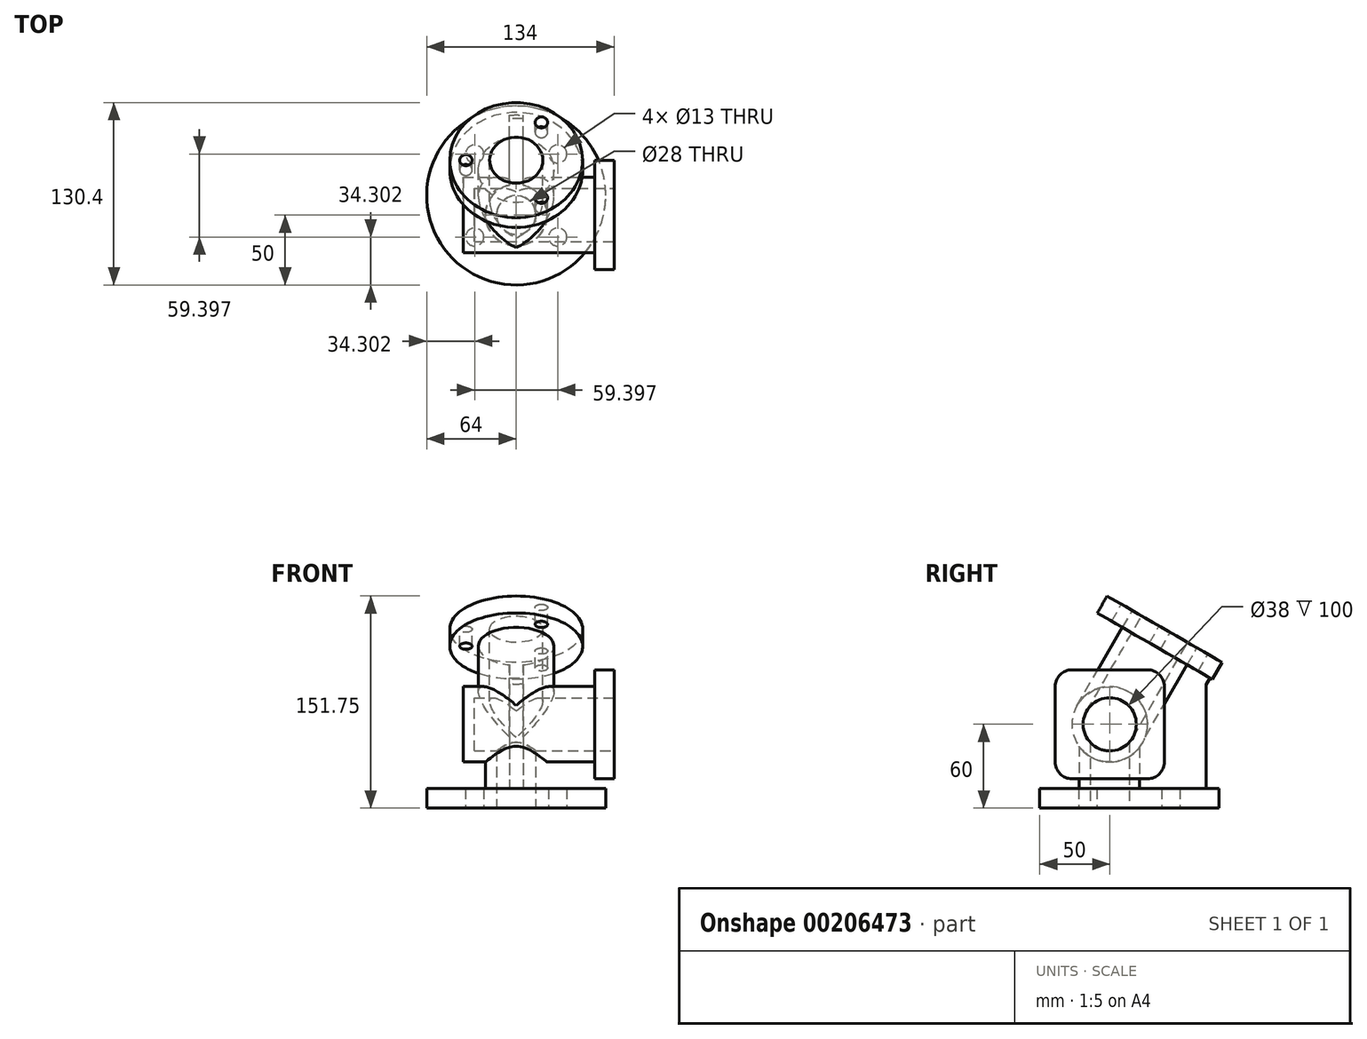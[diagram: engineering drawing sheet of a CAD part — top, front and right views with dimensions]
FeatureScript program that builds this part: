
annotation { "Feature Type Name" : "Feature", "Feature Type Description" : "" }
export const myFeature = defineFeature(function(context is Context, id is Id, definition is map)
    precondition{}
    {
        {
            var Q0;
            Q0=qCreatedBy(makeId("Top.planeOp"),FACE);
            var sketch = newSketch(context, id + "F0", { "sketchPlane" : qUnion([Q0])});
            skCircle(sketch, "E0", {"center": v(0, 0) * mm, "radius": 64 * mm});
            skCircle(sketch, "E1", {"center": v(29.7, 29.7) * mm, "radius": 6.5 * mm});
            skLineSegment(sketch, "E2", {"start": v(0, 0) * mm, "end": v(66.2, 66.2) * mm, "construction": true});
            skCircle(sketch, "E3", {"center": v(0, 0) * mm, "radius": 42 * mm, "construction": true});
            skCircle(sketch, "E4.1.0", {"center": v(-29.7, 29.7) * mm, "radius": 6.5 * mm});
            skCircle(sketch, "E4.2.0", {"center": v(-29.7, -29.7) * mm, "radius": 6.5 * mm});
            skCircle(sketch, "E4.3.0", {"center": v(29.7, -29.7) * mm, "radius": 6.5 * mm});
            skSolve(sketch);
        }
        {
            var Q0;
            Q0=makeQuery(id+"F0.imprint","IMPRINT",FACE,{"disambiguationData":[TD([[makeQuery(id+"F0.imprint","IMPRINT",EDGE,{"derivedFrom":sQuery(id+"F0.wireOp",EDGE,"E0")}),1.0]])]});
            extrude(context, id + "F1", {"entities" : qUnion([Q0]), "depth" : 14 * mm});
        }
        {
            var Q0;
            Q0=makeQuery(id+"F1.opExtrude","CAP_FACE",FACE,{"disambiguationData":[OSD([sQuery(id+"F0.wireOp",EDGE,"E0"),sQuery(id+"F0.wireOp",EDGE,"E1"),sQuery(id+"F0.wireOp",EDGE,"E4.1.0"),sQuery(id+"F0.wireOp",EDGE,"E4.2.0"),sQuery(id+"F0.wireOp",EDGE,"E4.3.0")])],"isStart":false});
            var sketch = newSketch(context, id + "F2", { "sketchPlane" : qUnion([Q0])});
            skCircle(sketch, "E5", {"center": v(0, -14) * mm, "radius": 22 * mm});
            skSolve(sketch);
        }
        {
            var Q0;
            Q0=makeQuery(id+"F2.imprint","IMPRINT",FACE,{"disambiguationData":[TD([[makeQuery(id+"F2.imprint","IMPRINT",EDGE,{"derivedFrom":sQuery(id+"F2.wireOp",EDGE,"E5")}),1.0]])]});
            extrude(context, id + "F3", {"entities" : qUnion([Q0]), "operationType" : NewBodyOperationType.ADD, "depth" : 46 * mm});
        }
        {
            var Q0;
            Q0=qCreatedBy(makeId("Right.planeOp"),FACE);
            cPlane(context, id + "F4", {"entities" : qUnion([Q0]), "cplaneType" : CPlaneType.OFFSET, "offset" : 70 * mm, "width" : 150 * mm, "height" : 150 * mm});
        }
        {
            var Q0;
            Q0=qCreatedBy(id+"F4.planeOp",FACE);
            var sketch = newSketch(context, id + "F5", { "sketchPlane" : qUnion([Q0])});
            skLineSegment(sketch, "E6.bottom", {"start": v(-41, 99) * mm, "end": v(13, 99) * mm});
            skLineSegment(sketch, "E6.top", {"start": v(-41, 21) * mm, "end": v(13, 21) * mm});
            skLineSegment(sketch, "E6.left", {"start": v(-53, 87) * mm, "end": v(-53, 33) * mm});
            skLineSegment(sketch, "E6.right", {"start": v(25, 87) * mm, "end": v(25, 33) * mm});
            skLineSegment(sketch, "E7", {"start": v(-14, -16.5) * mm, "end": v(-14, 110.8) * mm, "construction": true});
            skPoint(sketch, "E7.startSnap0", {"position": v(-14, 21) * mm});
            skLineSegment(sketch, "E8", {"start": v(-50.54, 60) * mm, "end": v(25, 60) * mm, "construction": true});
            skPoint(sketch, "E8.startSnap0", {"position": v(-53, 60) * mm});
            skPoint(sketch, "E9.visualSharp", {"position": v(-53, 99) * mm});
            skArc(sketch, "E9.filletArc", {"start": v(-41, 99) * mm, "mid": v(-49.49, 95.49) * mm, "end": v(-53, 87) * mm});
            skPoint(sketch, "E10.visualSharp", {"position": v(25, 99) * mm});
            skArc(sketch, "E10.filletArc", {"start": v(25, 87) * mm, "mid": v(21.49, 95.49) * mm, "end": v(13, 99) * mm});
            skPoint(sketch, "E11.visualSharp", {"position": v(25, 21) * mm});
            skArc(sketch, "E11.filletArc", {"start": v(13, 21) * mm, "mid": v(21.49, 24.51) * mm, "end": v(25, 33) * mm});
            skPoint(sketch, "E12.visualSharp", {"position": v(-53, 21) * mm});
            skArc(sketch, "E12.filletArc", {"start": v(-53, 33) * mm, "mid": v(-49.49, 24.51) * mm, "end": v(-41, 21) * mm});
            skCircle(sketch, "E13", {"center": v(-14, 60) * mm, "radius": 19 * mm});
            skSolve(sketch);
        }
        {
            var Q0;
            Q0=makeQuery(id+"F5.imprint","IMPRINT",FACE,{"disambiguationData":[TD([[makeQuery(id+"F5.imprint","IMPRINT",EDGE,{"derivedFrom":sQuery(id+"F5.wireOp",EDGE,"E6.bottom")}),-1.0]])]});
            extrude(context, id + "F6", {"entities" : qUnion([Q0]), "operationType" : NewBodyOperationType.ADD, "oppositeDirection" : true, "depth" : 14 * mm});
        }
        {
            var Q0;
            Q0=makeQuery(id+"F6.opExtrude","CAP_FACE",FACE,{"disambiguationData":[OSD([sQuery(id+"F5.wireOp",EDGE,"E6.bottom"),sQuery(id+"F5.wireOp",EDGE,"E6.top"),sQuery(id+"F5.wireOp",EDGE,"E6.left"),sQuery(id+"F5.wireOp",EDGE,"E6.right"),sQuery(id+"F5.wireOp",EDGE,"E9.filletArc"),sQuery(id+"F5.wireOp",EDGE,"E10.filletArc"),sQuery(id+"F5.wireOp",EDGE,"E11.filletArc"),sQuery(id+"F5.wireOp",EDGE,"E12.filletArc"),sQuery(id+"F5.wireOp",EDGE,"E13")])],"isStart":true});
            var sketch = newSketch(context, id + "F7", { "sketchPlane" : qUnion([Q0])});
            skCircle(sketch, "E14", {"center": v(-14, 60) * mm, "radius": 27 * mm});
            skSolve(sketch);
        }
        {
            var Q0;
            Q0 = qSketchRegion(id + "F7", true);
            extrude(context, id + "F8", {"entities" : qUnion([Q0]), "operationType" : NewBodyOperationType.ADD, "oppositeDirection" : true, "depth" : 108 * mm});
        }
        {
            var Q0;
            Q0=makeQuery(id+"F6.opExtrude","CAP_FACE",FACE,{"disambiguationData":[OSD([sQuery(id+"F5.wireOp",EDGE,"E6.bottom"),sQuery(id+"F5.wireOp",EDGE,"E6.top"),sQuery(id+"F5.wireOp",EDGE,"E6.left"),sQuery(id+"F5.wireOp",EDGE,"E6.right"),sQuery(id+"F5.wireOp",EDGE,"E9.filletArc"),sQuery(id+"F5.wireOp",EDGE,"E10.filletArc"),sQuery(id+"F5.wireOp",EDGE,"E11.filletArc"),sQuery(id+"F5.wireOp",EDGE,"E12.filletArc"),sQuery(id+"F5.wireOp",EDGE,"E13")])],"isStart":true});
            var sketch = newSketch(context, id + "F9", { "sketchPlane" : qUnion([Q0])});
            skCircle(sketch, "E15", {"center": v(-14, 60) * mm, "radius": 19 * mm});
            skSolve(sketch);
        }
        {
            var Q0;
            Q0=makeQuery(id+"F1.opExtrude","CAP_FACE",FACE,{"disambiguationData":[OSD([sQuery(id+"F0.wireOp",EDGE,"E0"),sQuery(id+"F0.wireOp",EDGE,"E1"),sQuery(id+"F0.wireOp",EDGE,"E4.1.0"),sQuery(id+"F0.wireOp",EDGE,"E4.2.0"),sQuery(id+"F0.wireOp",EDGE,"E4.3.0")])],"isStart":true});
            var sketch = newSketch(context, id + "F10", { "sketchPlane" : qUnion([Q0])});
            skCircle(sketch, "E16", {"center": v(0, 14) * mm, "radius": 14 * mm});
            skSolve(sketch);
        }
        {
            var Q0;
            Q0=makeQuery(id+"FyUdw1Quk5qUYTp_3.opBoolean","MERGE",FACE,{"derivedFrom":[makeQuery(id+"F6.opExtrude","CAP_FACE",FACE,{"disambiguationData":[OSD([sQuery(id+"F5.wireOp",EDGE,"E6.bottom"),sQuery(id+"F5.wireOp",EDGE,"E6.top"),sQuery(id+"F5.wireOp",EDGE,"E6.left"),sQuery(id+"F5.wireOp",EDGE,"E6.right"),sQuery(id+"F5.wireOp",EDGE,"E9.filletArc"),sQuery(id+"F5.wireOp",EDGE,"E10.filletArc"),sQuery(id+"F5.wireOp",EDGE,"E11.filletArc"),sQuery(id+"F5.wireOp",EDGE,"E12.filletArc"),sQuery(id+"F5.wireOp",EDGE,"E13")])],"isStart":true}),makeQuery(id+"F8.opExtrude","CAP_FACE",FACE,{"disambiguationData":[OSD([sQuery(id+"F7.wireOp",EDGE,"E14")])],"isStart":true})]});
            cPlane(context, id + "F11", {"entities" : qUnion([Q0]), "cplaneType" : CPlaneType.OFFSET, "offset" : 70 * mm, "oppositeDirection" : true, "width" : 150 * mm, "height" : 150 * mm});
        }
        {
            var Q0;
            Q0=qCreatedBy(id+"F11.planeOp",FACE);
            var sketch = newSketch(context, id + "F12", { "sketchPlane" : qUnion([Q0])});
            skLineSegment(sketch, "E17", {"start": v(-14, 60) * mm, "end": v(25.26, 128) * mm, "construction": true});
            skPoint(sketch, "E18", {"position": v(25.26, 128) * mm});
            skSolve(sketch);
        }
        {
            var Q0;
            Q0=sQuery(id+"F12.wireOp",VERTEX,"E18");
            var Q1;
            Q1=sQuery(id+"F12.wireOp",EDGE,"E17");
            cPlane(context, id + "F13", {"entities" : qUnion([Q0, Q1]), "cplaneType" : CPlaneType.LINE_POINT, "offset" : 25 * mm, "width" : 150 * mm, "height" : 150 * mm});
        }
        {
            var Q0;
            Q0=qCreatedBy(id+"F13.planeOp",FACE);
            var sketch = newSketch(context, id + "F14", { "sketchPlane" : qUnion([Q0])});
            skCircle(sketch, "E19", {"center": v(0, -42.12) * mm, "radius": 47.5 * mm});
            skCircle(sketch, "E20", {"center": v(-36, -42.12) * mm, "radius": 4.5 * mm});
            skCircle(sketch, "E21.1.0", {"center": v(18, -73.3) * mm, "radius": 4.5 * mm});
            skCircle(sketch, "E21.2.0", {"center": v(18, -10.95) * mm, "radius": 4.5 * mm});
            skSolve(sketch);
        }
        {
            var Q0;
            Q0=makeQuery(id+"F14.imprint","IMPRINT",FACE,{"disambiguationData":[TD([[makeQuery(id+"F14.imprint","IMPRINT",EDGE,{"derivedFrom":sQuery(id+"F14.wireOp",EDGE,"E19")}),1.0]])]});
            extrude(context, id + "F15", {"entities" : qUnion([Q0]), "operationType" : NewBodyOperationType.ADD, "oppositeDirection" : true, "depth" : 14 * mm});
        }
        {
            var Q0;
            Q0=makeQuery(id+"F15.opExtrude","CAP_FACE",FACE,{"disambiguationData":[OSD([sQuery(id+"F14.wireOp",EDGE,"E19"),sQuery(id+"F14.wireOp",EDGE,"E20"),sQuery(id+"F14.wireOp",EDGE,"E21.1.0"),sQuery(id+"F14.wireOp",EDGE,"E21.2.0")])],"isStart":false});
            var sketch = newSketch(context, id + "F16", { "sketchPlane" : qUnion([Q0])});
            skCircle(sketch, "E22", {"center": v(0, 42.12) * mm, "radius": 27 * mm});
            skSolve(sketch);
        }
        {
            var Q0;
            Q0=makeQuery(id+"F16.imprint","IMPRINT",FACE,{"disambiguationData":[TD([[makeQuery(id+"F16.imprint","IMPRINT",EDGE,{"derivedFrom":sQuery(id+"F16.wireOp",EDGE,"E22")}),1.0]])]});
            var Q1;
            Q1=makeQuery(id+"F8.opExtrude","SWEPT_FACE",FACE,{"disambiguationData":[OSD([sQuery(id+"F7.wireOp",EDGE,"E14")])]});
            var Q2;
            Q2=makeQuery(id+"F8.opExtrude","SWEPT_BODY",BODY,{"disambiguationData":[OSD([sQuery(id+"F7.wireOp",EDGE,"E14")])]});
            extrude(context, id + "F17", {"entities" : qUnion([Q0]), "operationType" : NewBodyOperationType.ADD, "endBound" : BoundingType.UP_TO_NEXT, "endBoundEntityFace" : qUnion([Q1]), "endBoundEntityBody" : qUnion([Q2]), "depth" : 25 * mm});
        }
        {
            var Q0;
            Q0=makeQuery(id+"F15.opExtrude","CAP_FACE",FACE,{"disambiguationData":[OSD([sQuery(id+"F14.wireOp",EDGE,"E19"),sQuery(id+"F14.wireOp",EDGE,"E20"),sQuery(id+"F14.wireOp",EDGE,"E21.1.0"),sQuery(id+"F14.wireOp",EDGE,"E21.2.0")])],"isStart":true});
            var sketch = newSketch(context, id + "F18", { "sketchPlane" : qUnion([Q0])});
            skCircle(sketch, "E23", {"center": v(0, -42.12) * mm, "radius": 19 * mm});
            skSolve(sketch);
        }
        {
            var Q0;
            Q0=makeQuery(id+"F15.opExtrude","CAP_FACE",FACE,{"disambiguationData":[OSD([sQuery(id+"F14.wireOp",EDGE,"E19"),sQuery(id+"F14.wireOp",EDGE,"E20"),sQuery(id+"F14.wireOp",EDGE,"E21.1.0"),sQuery(id+"F14.wireOp",EDGE,"E21.2.0")])],"isStart":false});
            var sketch = newSketch(context, id + "F19", { "sketchPlane" : qUnion([Q0])});
            skPoint(sketch, "E24", {"position": v(0, -5.38) * mm});
            skSolve(sketch);
        }
        {
            var Q0;
            Q0=makeQuery(id+"F1.opExtrude","CAP_FACE",FACE,{"disambiguationData":[OSD([sQuery(id+"F0.wireOp",EDGE,"E0"),sQuery(id+"F0.wireOp",EDGE,"E1"),sQuery(id+"F0.wireOp",EDGE,"E4.1.0"),sQuery(id+"F0.wireOp",EDGE,"E4.2.0"),sQuery(id+"F0.wireOp",EDGE,"E4.3.0")])],"isStart":false});
            var sketch = newSketch(context, id + "F20", { "sketchPlane" : qUnion([Q0])});
            skArc(sketch, "E25.0", {"start": v(5, 54.77) * mm, "mid": v(0, 55) * mm, "end": v(-5, 54.77) * mm});
            skArc(sketch, "E26.0", {"start": v(5, 7.42) * mm, "mid": v(0, 8) * mm, "end": v(-5, 7.42) * mm});
            skLineSegment(sketch, "E27", {"start": v(5, 7.42) * mm, "end": v(5, 54.77) * mm});
            skLineSegment(sketch, "E28", {"start": v(-5, 7.42) * mm, "end": v(-5, 54.77) * mm});
            skSolve(sketch);
        }
        {
            var Q0;
            Q0=makeQuery(id+"F20.imprint","IMPRINT",FACE,{"disambiguationData":[TD([[makeQuery(id+"F20.imprint","IMPRINT",EDGE,{"derivedFrom":sQuery(id+"F20.wireOp",EDGE,"E25.0")}),1.0]])]});
            extrude(context, id + "F21", {"entities" : qUnion([Q0]), "operationType" : NewBodyOperationType.ADD, "endBound" : BoundingType.UP_TO_NEXT, "depth" : 25 * mm});
        }
        {
            var Q0;
            Q0=makeQuery(id+"F19.imprint","IMPRINT",FACE,{"disambiguationData":[TD([[makeQuery(id+"F19.imprint","IMPRINT",EDGE,{"derivedFrom":makeQuery(id+"F15.opExtrude","CAP_EDGE",EDGE,{"disambiguationData":[OSD([sQuery(id+"F14.wireOp",EDGE,"E19")])],"isStart":false})}),-1.0]])]});
            var sketch = newSketch(context, id + "F22", { "sketchPlane" : qUnion([Q0])});
            skArc(sketch, "E29.0", {"start": v(-5, -3.1) * mm, "mid": v(0, -3.38) * mm, "end": v(5, -3.1) * mm});
            skLineSegment(sketch, "E30.0", {"start": v(-5, 15.6) * mm, "end": v(-5, -3.1) * mm});
            skLineSegment(sketch, "E31.0", {"start": v(5, 15.6) * mm, "end": v(5, -3.1) * mm});
            skPoint(sketch, "E32.orphan", {"position": v(5, -0.04) * mm});
            skArc(sketch, "E33.converted", {"start": v(-5, 15.6) * mm, "mid": v(0, 15.12) * mm, "end": v(5, 15.6) * mm});
            skPoint(sketch, "E34.orphan", {"position": v(-5, -0.04) * mm});
            skSolve(sketch);
        }
        {
            var Q0;
            Q0=makeQuery(id+"F22.imprint","IMPRINT",FACE,{"disambiguationData":[TD([[makeQuery(id+"F22.imprint","IMPRINT",EDGE,{"derivedFrom":sQuery(id+"F22.wireOp",EDGE,"E29.0")}),1.0]])]});
            extrude(context, id + "F23", {"entities" : qUnion([Q0]), "operationType" : NewBodyOperationType.ADD, "endBound" : BoundingType.UP_TO_NEXT, "depth" : 25 * mm});
        }
        {
            var Q0;
            Q0=qCreatedBy(makeId("Front.planeOp"),FACE);
            cPlane(context, id + "F24", {"entities" : qUnion([Q0]), "cplaneType" : CPlaneType.OFFSET, "offset" : 14 * mm, "width" : 150 * mm, "height" : 150 * mm});
        }
        {
            var Q0;
            Q0=makeQuery(id+"F9.imprint","IMPRINT",FACE,{"disambiguationData":[TD([[makeQuery(id+"F9.imprint","IMPRINT",EDGE,{"derivedFrom":sQuery(id+"F9.wireOp",EDGE,"E15")}),1.0]])]});
            extrude(context, id + "F25", {"entities" : qUnion([Q0]), "operationType" : NewBodyOperationType.REMOVE, "oppositeDirection" : true, "depth" : 100 * mm});
        }
        {
            var Q0;
            Q0=makeQuery(id+"F18.imprint","IMPRINT",FACE,{"disambiguationData":[TD([[makeQuery(id+"F18.imprint","IMPRINT",EDGE,{"derivedFrom":sQuery(id+"F18.wireOp",EDGE,"E23")}),1.0]])]});
            extrude(context, id + "F26", {"entities" : qUnion([Q0]), "operationType" : NewBodyOperationType.REMOVE, "endBound" : BoundingType.UP_TO_NEXT, "oppositeDirection" : true, "depth" : 25 * mm});
        }
        {
            var Q0;
            Q0=makeQuery(id+"F10.imprint","IMPRINT",FACE,{"disambiguationData":[TD([[makeQuery(id+"F10.imprint","IMPRINT",EDGE,{"derivedFrom":sQuery(id+"F10.wireOp",EDGE,"E16")}),1.0]])]});
            extrude(context, id + "F28", {"entities" : qUnion([Q0]), "operationType" : NewBodyOperationType.REMOVE, "oppositeDirection" : true, "depth" : 60 * mm});
        }
    });
